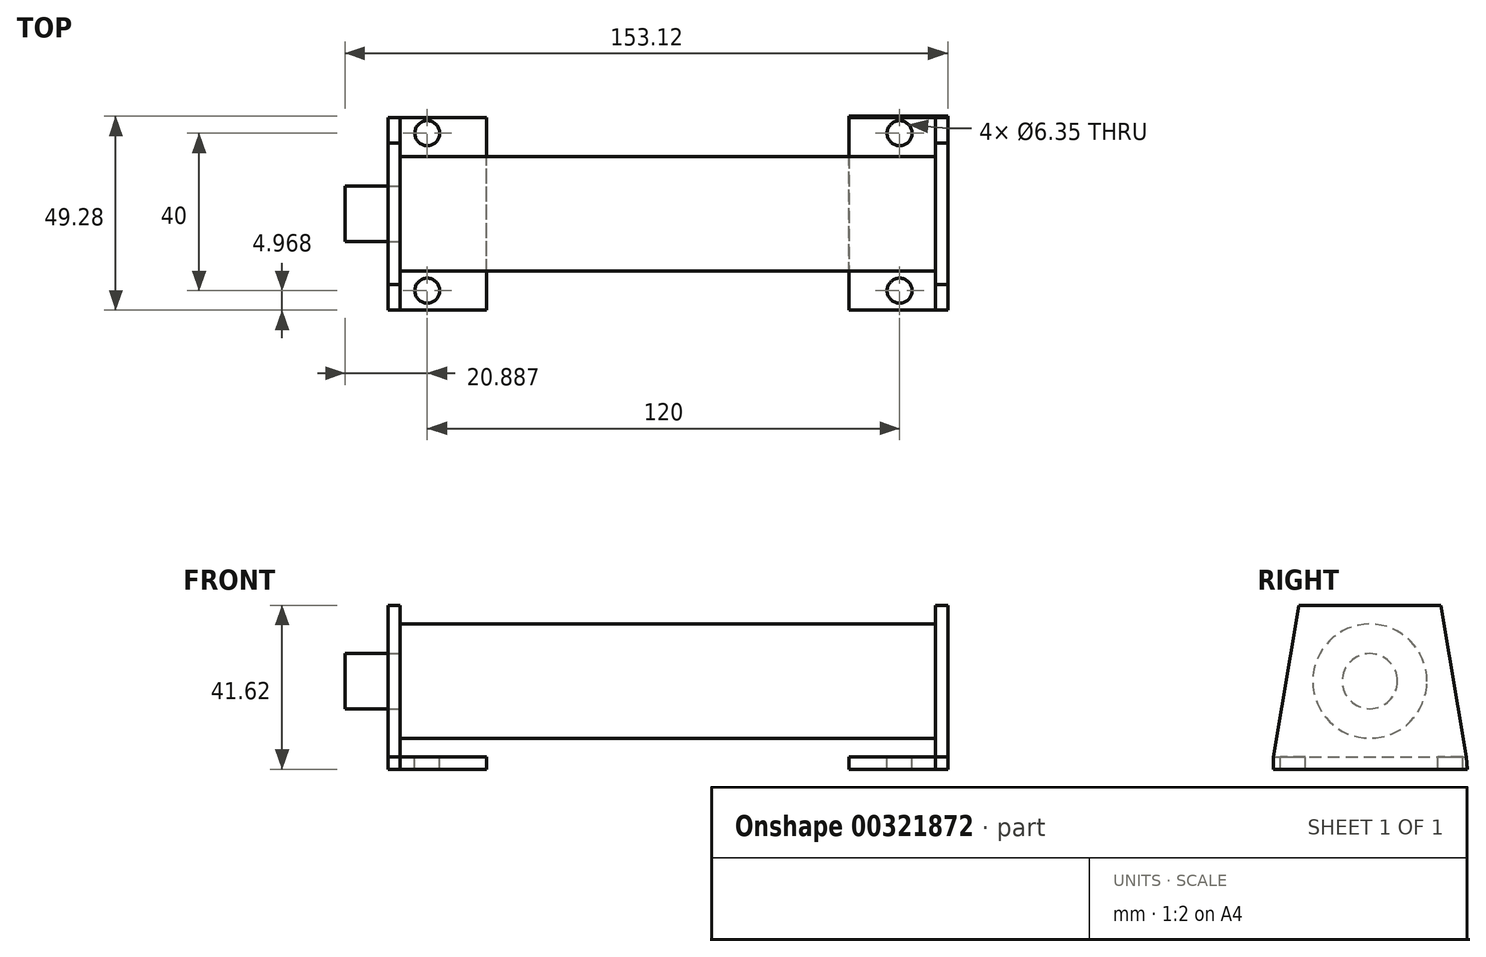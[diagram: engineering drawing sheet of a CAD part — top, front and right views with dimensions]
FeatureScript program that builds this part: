
annotation { "Feature Type Name" : "Feature", "Feature Type Description" : "" }
export const myFeature = defineFeature(function(context is Context, id is Id, definition is map)
    precondition{}
    {
        {
            var Q0;
            Q0=qCreatedBy(makeId("Right.planeOp"),FACE);
            var sketch = newSketch(context, id + "F0", { "sketchPlane" : qUnion([Q0])});
            skCircle(sketch, "E0", {"center": v(0, 0) * mm, "radius": 14.5 * mm});
            skSolve(sketch);
        }
        {
            var Q0;
            Q0=makeQuery(id+"F0.imprint","IMPRINT",FACE,{"disambiguationData":[TD([[makeQuery(id+"F0.imprint","IMPRINT",EDGE,{"derivedFrom":sQuery(id+"F0.wireOp",EDGE,"E0")}),1.0]])]});
            extrude(context, id + "F1", {"entities" : qUnion([Q0]), "depth" : 136 * mm});
        }
        {
            var Q0;
            Q0=qCreatedBy(makeId("Right.planeOp"),FACE);
            var sketch = newSketch(context, id + "F2", { "sketchPlane" : qUnion([Q0])});
            skCircle(sketch, "E1", {"center": v(0, 0) * mm, "radius": 7 * mm});
            skSolve(sketch);
        }
        {
            var Q0;
            Q0=makeQuery(id+"F2.imprint","IMPRINT",FACE,{"disambiguationData":[TD([[makeQuery(id+"F2.imprint","IMPRINT",EDGE,{"derivedFrom":sQuery(id+"F2.wireOp",EDGE,"E1")}),1.0]])]});
            var Q1;
            Q1=sQuery(id+"F2.wireOp",EDGE,"E1");
            extrude(context, id + "F3", {"entities" : qUnion([Q0]), "surfaceEntities" : qUnion([Q1]), "oppositeDirection" : true, "depth" : 14 * mm});
        }
        {
            var Q0;
            Q0=qCreatedBy(makeId("Right.planeOp"),FACE);
            var sketch = newSketch(context, id + "F4", { "sketchPlane" : qUnion([Q0])});
            skLineSegment(sketch, "E2", {"start": v(0, 19.25) * mm, "end": v(0, -19.25) * mm});
            skLineSegment(sketch, "E3", {"start": v(-18, 19.25) * mm, "end": v(18, 19.25) * mm});
            skLineSegment(sketch, "E4", {"start": v(-24.5, -19.25) * mm, "end": v(24.5, -19.25) * mm});
            skLineSegment(sketch, "E5", {"start": v(-18, 19.25) * mm, "end": v(-24.5, -19.25) * mm});
            skLineSegment(sketch, "E6", {"start": v(18, 19.25) * mm, "end": v(24.5, -19.25) * mm});
            skLineSegment(sketch, "E7", {"start": v(-24.5, -19.25) * mm, "end": v(-24.5, -22.37) * mm});
            skLineSegment(sketch, "E8", {"start": v(-24.5, -22.37) * mm, "end": v(24.5, -22.37) * mm});
            skLineSegment(sketch, "E9", {"start": v(24.5, -22.37) * mm, "end": v(24.5, -19.25) * mm});
            skSolve(sketch);
        }
        {
            var Q0;
            {var subQ0=sQuery(id+"F4.wireOp",EDGE,"E7");Q0=makeQuery(id+"F4.imprint","IMPRINT",FACE,{"disambiguationData":[TD([[makeQuery(id+"F4.imprint","IMPRINT",EDGE,{"derivedFrom":subQ0}),1.0]])]});}
            extrude(context, id + "F5", {"entities" : qUnion([Q0]), "operationType" : NewBodyOperationType.ADD, "depth" : 22 * mm});
        }
        {
            var Q0;
            Q0=qCreatedBy(makeId("Right.planeOp"),FACE);
            cPlane(context, id + "F6", {"entities" : qUnion([Q0]), "cplaneType" : CPlaneType.OFFSET, "offset" : 136 * mm, "width" : 152.4 * mm, "height" : 152.4 * mm});
        }
        {
            var Q0;
            Q0=qCreatedBy(id+"F6.planeOp",FACE);
            var sketch = newSketch(context, id + "F7", { "sketchPlane" : qUnion([Q0])});
            skLineSegment(sketch, "E10", {"start": v(-18, 19.25) * mm, "end": v(18, 19.25) * mm});
            skLineSegment(sketch, "E11", {"start": v(18, 19.25) * mm, "end": v(0, 19.25) * mm});
            skLineSegment(sketch, "E12", {"start": v(0, 19.25) * mm, "end": v(0, -19.25) * mm});
            skLineSegment(sketch, "E13", {"start": v(18, 19.25) * mm, "end": v(24.5, -19.25) * mm});
            skLineSegment(sketch, "E14", {"start": v(24.5, -19.25) * mm, "end": v(-24.5, -19.25) * mm});
            skLineSegment(sketch, "E15", {"start": v(-24.5, -19.25) * mm, "end": v(-18, 19.25) * mm});
            skLineSegment(sketch, "E16", {"start": v(-24.5, -19.25) * mm, "end": v(-24.5, -22.37) * mm});
            skLineSegment(sketch, "E17", {"start": v(-24.5, -22.37) * mm, "end": v(24.78, -22.37) * mm});
            skLineSegment(sketch, "E18", {"start": v(24.78, -22.37) * mm, "end": v(24.5, -19.25) * mm});
            skSolve(sketch);
        }
        {
            var Q0;
            {var subQ0=sQuery(id+"F7.wireOp",EDGE,"E16");Q0=makeQuery(id+"F7.imprint","IMPRINT",FACE,{"disambiguationData":[TD([[makeQuery(id+"F7.imprint","IMPRINT",EDGE,{"derivedFrom":subQ0}),1.0]])]});}
            extrude(context, id + "F8", {"entities" : qUnion([Q0]), "operationType" : NewBodyOperationType.ADD, "oppositeDirection" : true, "depth" : 22 * mm});
        }
        {
            var Q0;
            Q0 = qSketchRegion(id + "F7", true);
            extrude(context, id + "F9", {"entities" : qUnion([Q0]), "depth" : 3.12 * mm});
        }
        {
            var Q0;
            Q0=qCreatedBy(makeId("Top.planeOp"),FACE);
            cPlane(context, id + "F10", {"entities" : qUnion([Q0]), "cplaneType" : CPlaneType.OFFSET, "offset" : 19.25 * mm, "oppositeDirection" : true, "width" : 152.4 * mm, "height" : 152.4 * mm});
        }
        {
            var Q0;
            Q0 = qSketchRegion(id + "F4", true);
            extrude(context, id + "F11", {"entities" : qUnion([Q0]), "oppositeDirection" : true, "depth" : 3.12 * mm});
        }
        {
            var Q0;
            Q0=qCreatedBy(id+"F10.planeOp",FACE);
            var sketch = newSketch(context, id + "F12", { "sketchPlane" : qUnion([Q0])});
            skPoint(sketch, "E19", {"position": v(6.89, -19.53) * mm});
            skPoint(sketch, "E20", {"position": v(6.89, 20.47) * mm});
            skPoint(sketch, "E21", {"position": v(126.89, 20.47) * mm});
            skCircle(sketch, "E22", {"center": v(126.89, -19.53) * mm, "radius": 3.17 * mm});
            skSolve(sketch);
        }
        {
            var Q0;
            Q0=sQuery(id+"F12.wireOp",VERTEX,"E19");
            var Q1;
            Q1=sQuery(id+"F12.wireOp",VERTEX,"E20");
            var Q2;
            Q2=sQuery(id+"F12.wireOp",VERTEX,"f817f15e-d51e-497c-bf8d-147d22056cfb");
            var Q3;
            Q3=sQuery(id+"F12.wireOp",VERTEX,"E21");
            var Q4;
            Q4=sQuery(id+"F12.wireOp",VERTEX,"E22.center");
            var Q5;
            Q5=makeQuery(id+"F5.opExtrude","SWEPT_BODY",BODY,{"disambiguationData":[OSD([sQuery(id+"F4.wireOp",EDGE,"E4"),sQuery(id+"F4.wireOp",EDGE,"E7"),sQuery(id+"F4.wireOp",EDGE,"E8"),sQuery(id+"F4.wireOp",EDGE,"E9")])]});
            var Q6;
            Q6=makeQuery(id+"F8.opExtrude","SWEPT_BODY",BODY,{"disambiguationData":[OSD([sQuery(id+"F7.wireOp",EDGE,"E14"),sQuery(id+"F7.wireOp",EDGE,"E16"),sQuery(id+"F7.wireOp",EDGE,"E17"),sQuery(id+"F7.wireOp",EDGE,"E18")])]});
            hole(context, id + "F13", {"style" : HoleStyle.SIMPLE, "endStyle" : HoleEndStyle.THROUGH, "holeDiameter" : 6.35 * mm, "tappedDepth" : 12.7 * mm, "tapClearance" : 3, "locations" : qUnion([Q0, Q1, Q2, Q3, Q4]), "scope" : qUnion([Q5, Q6])});
        }
    });
